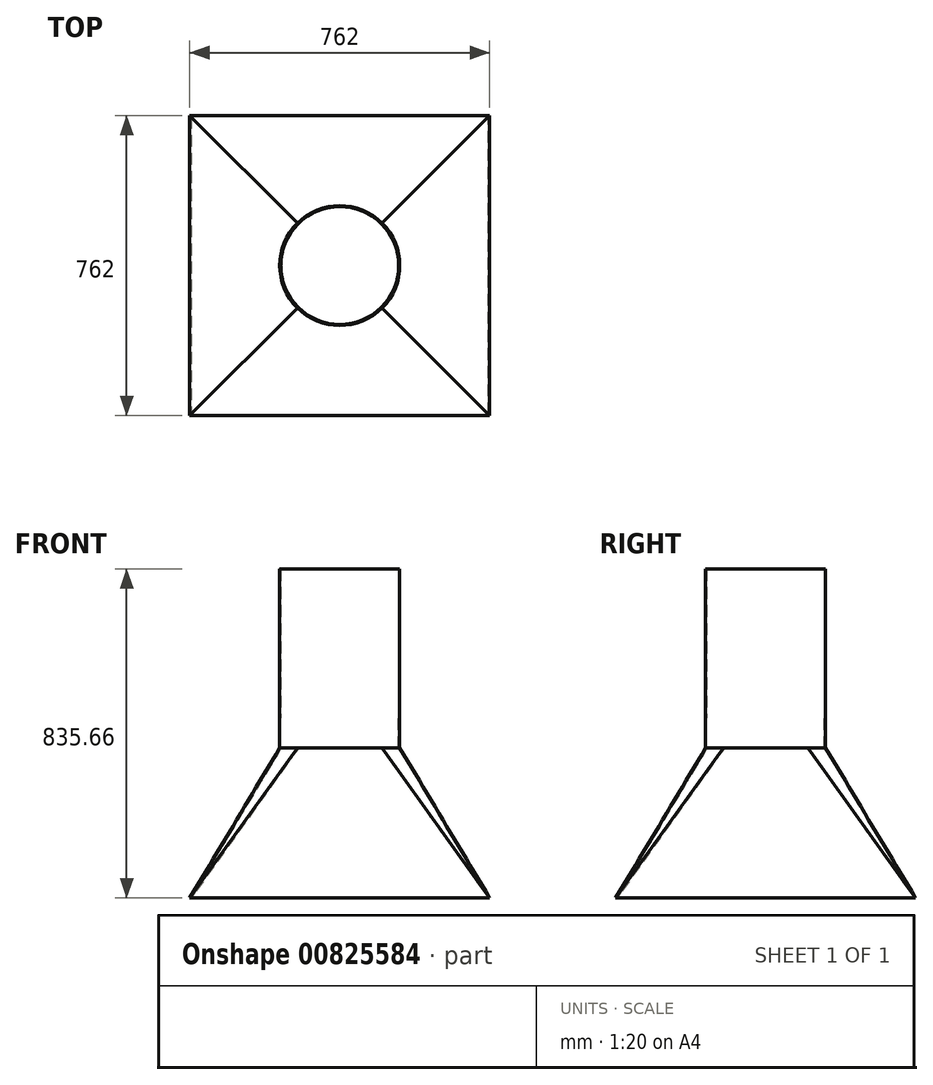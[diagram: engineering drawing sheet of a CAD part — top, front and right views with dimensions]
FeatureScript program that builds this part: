
annotation { "Feature Type Name" : "Feature", "Feature Type Description" : "" }
export const myFeature = defineFeature(function(context is Context, id is Id, definition is map)
    precondition{}
    {
        {
            var Q0;
            Q0=qCreatedBy(makeId("Top.planeOp"),FACE);
            var sketch = newSketch(context, id + "F0", { "sketchPlane" : qUnion([Q0])});
            skLineSegment(sketch, "E0.bottom", {"start": v(0, 0) * mm, "end": v(762, 0) * mm});
            skLineSegment(sketch, "E0.top", {"start": v(0, 762) * mm, "end": v(762, 762) * mm});
            skLineSegment(sketch, "E0.left", {"start": v(0, 0) * mm, "end": v(0, 762) * mm});
            skLineSegment(sketch, "E0.right", {"start": v(762, 0) * mm, "end": v(762, 762) * mm});
            skSolve(sketch);
        }
        {
            var Q0;
            Q0=qCreatedBy(makeId("Top.planeOp"),FACE);
            cPlane(context, id + "F1", {"entities" : qUnion([Q0]), "cplaneType" : CPlaneType.OFFSET, "offset" : 381 * mm, "width" : 152.4 * mm, "height" : 152.4 * mm});
        }
        {
            var Q0;
            Q0=qCreatedBy(id+"F1.planeOp",FACE);
            var sketch = newSketch(context, id + "F2", { "sketchPlane" : qUnion([Q0])});
            skCircle(sketch, "E1", {"center": v(381, 381) * mm, "radius": 152.4 * mm});
            skSolve(sketch);
        }
        {
            var Q0;
            Q0=makeQuery(id+"F0.imprint","IMPRINT",FACE,{"disambiguationData":[TD([[makeQuery(id+"F0.imprint","IMPRINT",EDGE,{"derivedFrom":sQuery(id+"F0.wireOp",EDGE,"E0.bottom")}),1.0]])]});
            var Q1;
            Q1=makeQuery(id+"F2.imprint","IMPRINT",FACE,{"disambiguationData":[TD([[makeQuery(id+"F2.imprint","IMPRINT",EDGE,{"derivedFrom":sQuery(id+"F2.wireOp",EDGE,"E1")}),1.0]])]});
            loft(context, id + "F3", {"sheetProfilesArray" : [{ "sheetProfileEntities" : qUnion([Q0]) }, { "sheetProfileEntities" : qUnion([Q1]) }]});
        }
        {
            var Q0;
            Q0=makeQuery(id+"F3.opLoft","CAP_FACE",FACE,{"disambiguationData":[OSD([makeQuery(id+"F2.imprint","IMPRINT",FACE,{"disambiguationData":[TD([[makeQuery(id+"F2.imprint","IMPRINT",EDGE,{"derivedFrom":sQuery(id+"F2.wireOp",EDGE,"E1")}),1.0]])]})])],"isStart":true});
            extrude(context, id + "F4", {"entities" : qUnion([Q0]), "operationType" : NewBodyOperationType.ADD, "depth" : 76.2 * mm});
        }
        {
            var Q0;
            Q0=makeQuery(id+"F3.opLoft","CAP_FACE",FACE,{"disambiguationData":[OSD([makeQuery(id+"F0.imprint","IMPRINT",FACE,{"disambiguationData":[TD([[makeQuery(id+"F0.imprint","IMPRINT",EDGE,{"derivedFrom":sQuery(id+"F0.wireOp",EDGE,"E0.bottom")}),1.0]])]})])],"isStart":true});
            var Q1;
            Q1=makeQuery(id+"F4.opExtrude","CAP_FACE",FACE,{"disambiguationData":[OSD([makeQuery(id+"F2.imprint","IMPRINT",FACE,{"disambiguationData":[TD([[makeQuery(id+"F2.imprint","IMPRINT",EDGE,{"derivedFrom":sQuery(id+"F2.wireOp",EDGE,"E1")}),1.0]])]})])],"isStart":false});
            shell(context, id + "F5", {"entities" : qUnion([Q0, Q1]), "thickness" : 2.54 * mm});
        }
        {
            var Q0;
            Q0=makeQuery(id+"F4.opExtrude","CAP_FACE",FACE,{"disambiguationData":[OSD([makeQuery(id+"F2.imprint","IMPRINT",FACE,{"disambiguationData":[TD([[makeQuery(id+"F2.imprint","IMPRINT",EDGE,{"derivedFrom":sQuery(id+"F2.wireOp",EDGE,"E1")}),1.0]])]})])],"isStart":false});
            extrude(context, id + "F6", {"entities" : qUnion([Q0]), "operationType" : NewBodyOperationType.ADD, "depth" : 378.46 * mm, "offsetDistance" : 25.4 * mm});
        }
    });
